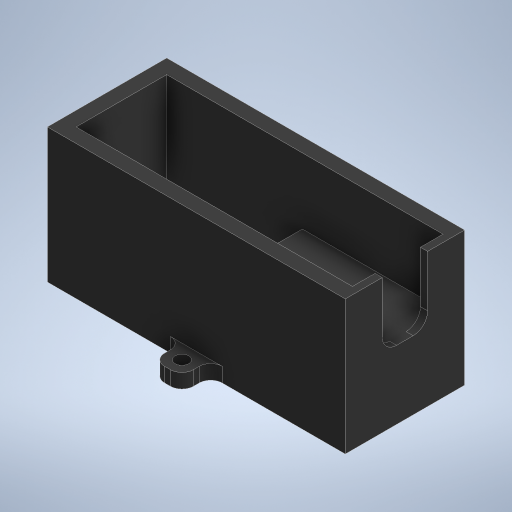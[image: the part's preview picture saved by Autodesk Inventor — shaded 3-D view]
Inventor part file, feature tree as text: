
AUTODESK INVENTOR PART (.ipt)
format: ipt  version: 2024 (Build 280153000, 153)  size: 308,736 bytes
history: native  units: in
note: dims shown in document units (in); Inventor stores cm internally (conversion verified against a paired STEP export)
features: extrude x5, sketch x5, fillet x2, plane x1, mirror x1, projected_geometry x1
ambient origin geometry x8: Origin, YZ Plane, XZ Plane, XY Plane, X Axis, Y Axis, Z Axis, Center Point
bodies: Solid1 (feature_tree)
feature tree (15):
  extrude  "Extrusion1"  Depth=0.47in
  sketch  "Sketch2"  dims[d2=1.1417in d3=1.6142in]
  plane  "Work Plane1"
  extrude  "Extrusion2"  Depth=1.1417in
  mirror  "Mirror1"
  extrude  "Extrusion3"  Depth=0.063in
  fillet  "Fillet1"  Radius=0.125in
  extrude  "Extrusion4"  Depth=0.125in
  fillet  "Fillet2"  Radius=0.7874in
  extrude  "Extrusion5"  Depth=0.125in TaperAngle=0.0deg
  sketch  "Sketch1"  dims[d0=1.2598in d1=0.47in]
  sketch  "Sketch3"  dims[d4=0.4724in d5=0.063in d7=0.125in]
  sketch  "Sketch4"  dims[d8=0.125in d9=0.125in d10=0.7874in d11=0.0in]
  sketch  "Sketch5"  dims[d12=-0.3937in d13=0.125in d14=0.0in d15=0.1969in d16=0.1969in d17=0.125in d18=0.0in d19=0.125in d20=0.125in d21=0.25in d22=0.125in d23=0.1181in d24=0.125in d25=0.0in d26=0.1in d27=0.1in d28=0.0in]
  projected_geometry  "Projected Loop1"
